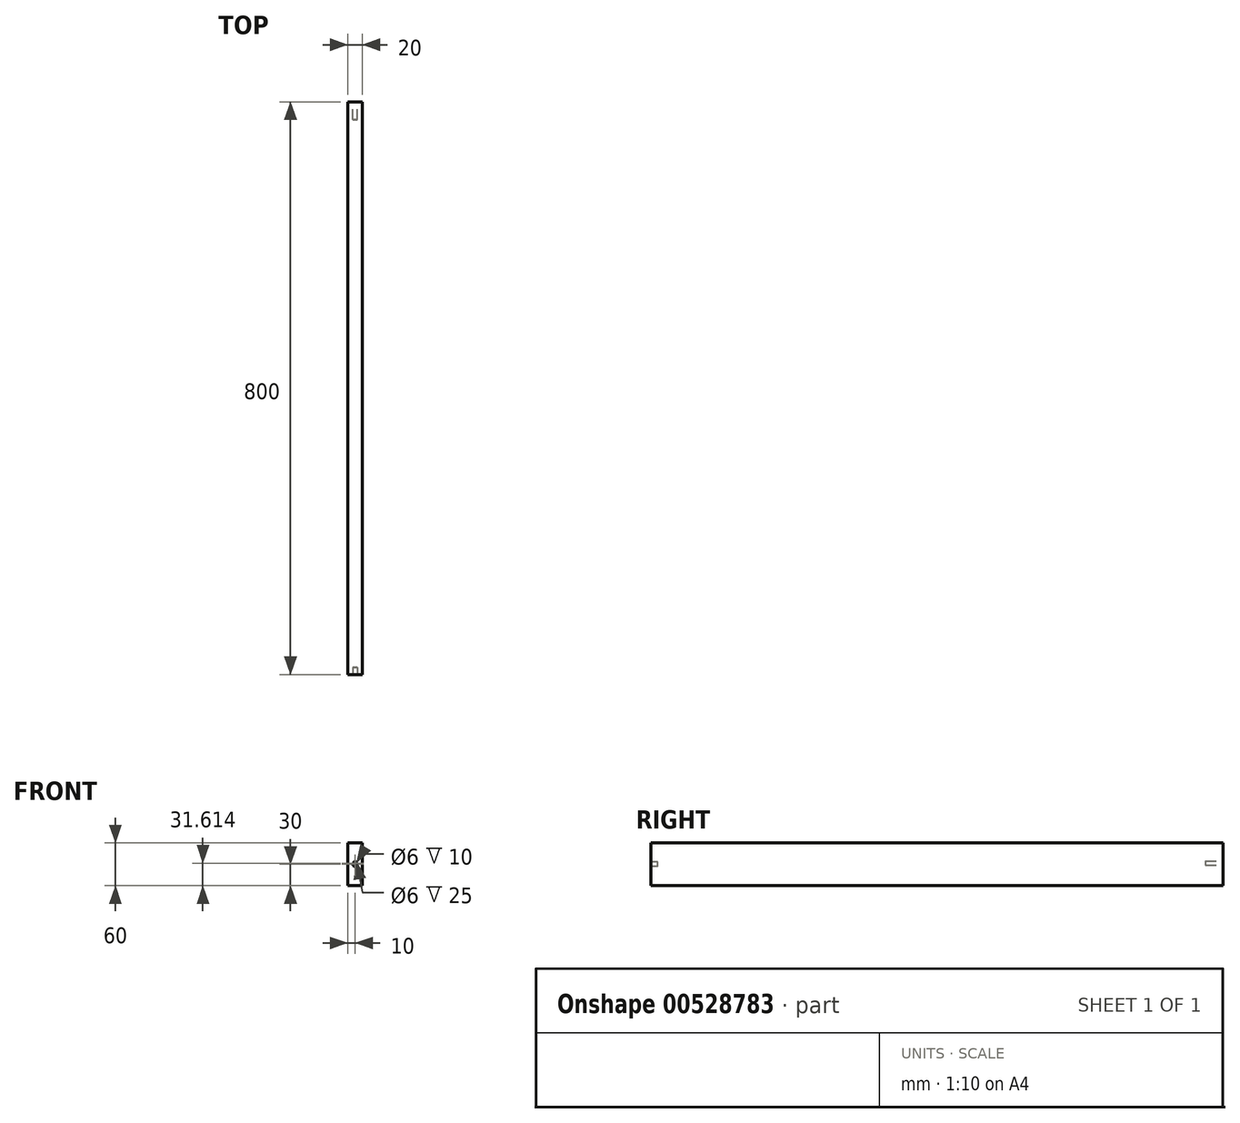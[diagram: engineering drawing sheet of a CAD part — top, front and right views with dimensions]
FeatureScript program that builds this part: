
annotation { "Feature Type Name" : "Feature", "Feature Type Description" : "" }
export const myFeature = defineFeature(function(context is Context, id is Id, definition is map)
    precondition{}
    {
        {
            var Q0;
            Q0=qCreatedBy(makeId("Front.planeOp"),FACE);
            var sketch = newSketch(context, id + "F0", { "sketchPlane" : qUnion([Q0])});
            skLineSegment(sketch, "E0.bottom", {"start": v(0, 0) * mm, "end": v(20, 0) * mm});
            skLineSegment(sketch, "E0.top", {"start": v(0, 60) * mm, "end": v(20, 60) * mm});
            skLineSegment(sketch, "E0.left", {"start": v(0, 0) * mm, "end": v(0, 60) * mm});
            skLineSegment(sketch, "E0.right", {"start": v(20, 0) * mm, "end": v(20, 60) * mm});
            skSolve(sketch);
        }
        {
            var Q0;
            Q0 = qSketchRegion(id + "F0", true);
            extrude(context, id + "F1", {"entities" : qUnion([Q0]), "depth" : 800 * mm, "offsetDistance" : 25 * mm, "symmetric" : true});
        }
        {
            var Q0;
            Q0=makeQuery(id+"F1.opExtrude","CAP_FACE",FACE,{"disambiguationData":[OSD([sQuery(id+"F0.wireOp",EDGE,"E0.bottom"),sQuery(id+"F0.wireOp",EDGE,"E0.top"),sQuery(id+"F0.wireOp",EDGE,"E0.left"),sQuery(id+"F0.wireOp",EDGE,"E0.right")])],"isStart":false});
            var sketch = newSketch(context, id + "F2", { "sketchPlane" : qUnion([Q0])});
            skCircle(sketch, "E1", {"center": v(10, 30) * mm, "radius": 3 * mm});
            skPoint(sketch, "E1.centerSnap0", {"position": v(0, 30) * mm});
            skPoint(sketch, "E1.centerSnap1", {"position": v(10, 60) * mm});
            skSolve(sketch);
        }
        {
            var Q0;
            Q0 = qSketchRegion(id + "F2", true);
            extrude(context, id + "F3", {"entities" : qUnion([Q0]), "operationType" : NewBodyOperationType.REMOVE, "oppositeDirection" : true, "depth" : 10 * mm, "offsetDistance" : 25 * mm});
        }
        {
            var Q0;
            Q0=makeQuery(id+"F1.opExtrude","CAP_FACE",FACE,{"disambiguationData":[OSD([sQuery(id+"F0.wireOp",EDGE,"E0.bottom"),sQuery(id+"F0.wireOp",EDGE,"E0.top"),sQuery(id+"F0.wireOp",EDGE,"E0.left"),sQuery(id+"F0.wireOp",EDGE,"E0.right")])],"isStart":true});
            var sketch = newSketch(context, id + "F4", { "sketchPlane" : qUnion([Q0])});
            skCircle(sketch, "E2", {"center": v(-10, 31.61) * mm, "radius": 3 * mm});
            skPoint(sketch, "E2.centerSnap0", {"position": v(-10, 60) * mm});
            skSolve(sketch);
        }
        {
            var Q0;
            Q0 = qSketchRegion(id + "F4", true);
            extrude(context, id + "F5", {"entities" : qUnion([Q0]), "operationType" : NewBodyOperationType.REMOVE, "oppositeDirection" : true, "depth" : 25 * mm, "offsetDistance" : 25 * mm});
        }
    });
